# Revit family: JLG_Site_LowLevelAccess_ECOLIFT15_ORANGEa
name_source: partatom
category: Site
revit_build: Autodesk Revit 2017 (Build: 20190508_0315(x64)
units: mm (PartAtom-declared; Revit-internal decimal feet)

## family parameters
Always vertical = Yes
Cut with Voids When Loaded = No
OmniClass Number = 23.40.00.00
OmniClass Title = Equipment and Furnishings
Part Type = Normal
Round Connector Dimension = Use Diameter
Shared = No
Work Plane-Based = No

## types (1)
- ECOLIFT15 - ORANGE
    Assembly Code = E1030100
    AssetType = Movable
    BIMObjectName = JLG_Site_LowLevelAccess_ECOLIFT15_ORANGE
    BasketDimensions = 0.72 m x 0.60 m ( 2 ft 4 in x 1 ft-11.5 in)
    BasketSize = 0.72 m x 0.60 m ( 2 ft 4 in x 1ft 11.5 in)
    ClassificationName = Uniclass2015
    ClassificationValue = TE_30_30_10_60
    DocumentationCertificates = https://www.bimstore.co
    DocumentationInstallationGuide = https://www.bimstore.co
    DocumentationLiterature = https://www.bimstore.co
    DocumentationMaintenance = https://www.bimstore.co
    DocumentationTechnical = https://www.bimstore.co
    DurationUnit = Years
    Ecolift = Ecolift 1.5
    ExpectedLife = 0
    IfcExportAs = IfcTransportElement
    IfcExportType = IfcTransportElementType
    IntuitiveToOperate = Turn handle to operate
    Keynote = X
    MachineWeightANSI = 180 kg (397 lbs)
    MachineWeightCE = 180 kg (397 lbs)
    Manufacturer = JLG
    ManufacturerName = JLG
    Material = Steel
    MaximumGradientForOperation = 0 degrees
    MaximumManualForce = 200N
    MaximumWindForce = Internal use only
    Model = Low Level Access - ECOLIFT15 - ORANGE
    ModelNumber = Low Level Access - ECOLIFT15 - ORANGE
    ModelReference = Low Level Access
    NBSDescription = Lift platforms
    NBSObjectName = JLG - Lift platforms
    NominalDepth = 0 mm  [stored 0 ft]
    NominalHeight = 0 mm  [stored 0 ft]
    NominalLength = 0 mm  [stored 0 ft]
    ProductionYear = 2020
    RaisedPlatformHeight = 1.50m (4 ft 11 in)
    SafeWorkingLoadANSI = 149.68kg (330 lbs)
    SafeWorkingLoadCE = 150 kg (331 lbs)
    Type Comments = JLG_Site_LowLevelAccess_ECOLIFT15_ORANGE
    TypeName = JLG_Site_LowLevelAccess_ECOLIFT15_ORANGE
    URL = https://www.jlg.com
    UniqueModelReferenceFAPL = 1001214402
    WarrantyDurationLabor = 0
    WarrantyDurationParts = 0
    WarrantyDurationUnit = Years
    WarrantyGuarantorLabor = https://www.jlg.com
    WarrantyGuarantorParts = https://www.jlg.com
    WorkingHeightANSI = 3.33 m (10 ft  11 in)
    WorkingHeightCE = 3.50m (11 ft 6 in)
    _BSBibleVersion = 16
    _BimSpecGuid = 0
    _CurrentRevision = 1
    _DistributedBy = https://www.bimstore.co
    _ObjectUserGuide = https://www.bimstore.co

note: [stored X ft] marks values corroborated as IEEE doubles in the binary element streams (Revit-internal decimal feet)

## geometry (parser evidence)
native form markers: Sweep x4
no freeform markers — native parametric forms only
